AUTODESK INVENTOR PART (.ipt)
format: ipt  version: 2017 (Build 210142000, 142)  size: 140,288 bytes
history: native  units: mm
features: sketch x3, extrude x2, hole x1
ambient origin geometry x8: Origin, YZ Plane, XZ Plane, XY Plane, X Axis, Y Axis, Z Axis, Center Point
bodies: Solid1 (feature_tree)
feature tree (6):
  extrude  "Extrusion1"  Depth=5.0mm
  hole  "Hole1"  [1 undecoded]
  extrude  "Extrusion2"  Depth=5.0mm
  sketch  "Sketch1"  dims[d0=5.0mm d1=5.0mm]
  sketch  "Sketch2"  dims[d2=40.707766mm d3=5.0mm]
  sketch  "Sketch3"  dims[d4=25.384678mm d5=29.129655mm d6=53.5mm d7=5.0mm d8=0.0mm d9=3.302mm d10=8.331mm d11=4.0mm d12=2.0mm d13=90.0deg d14=12.3mm d15=20.594885mm d16=2.0mm d17=90.0mm d19=180.0deg d21=5.0mm d22=0.0mm]
note: 1 required parameter value undecoded (feature->parameter linkage not recoverable at this tier; creation-order binding heuristic only, values carry confidence <= 0.55)
